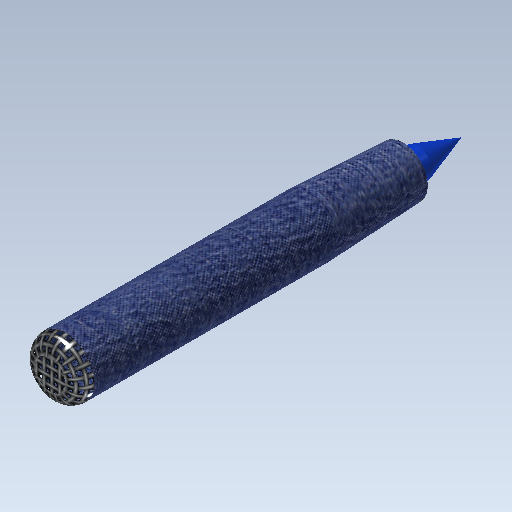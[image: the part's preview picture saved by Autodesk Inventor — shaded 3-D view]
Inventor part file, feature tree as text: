
AUTODESK INVENTOR PART (.ipt)
format: ipt  version: 2021.3 (Build 253353000, 353)  size: 197,120 bytes
history: native  units: mm
features: extrude x2, chamfer x2, sketch x2, fillet x1
ambient origin geometry x8: Origin, YZ Plane, XZ Plane, XY Plane, X Axis, Y Axis, Z Axis, Center Point
bodies: Solid1 (feature_tree)
feature tree (7):
  extrude  "Extrusion1"  Depth=120.0mm TaperAngle=0.0deg
  extrude  "Extrusion2"  Depth=5.0mm TaperAngle=0.0deg
  chamfer  "Chamfer1"  Distance=5.0mm Angle=45.0deg
  chamfer  "Chamfer2"  Distance=1.5mm Angle=45.0deg
  fillet  "Fillet1"  Radius=5.0mm
  sketch  "Sketch1"  dims[d0=20.0mm d1=120.0mm d2=0.0mm]
  sketch  "Sketch2"  dims[d3=10.0mm d4=20.0mm d5=0.0mm d6=5.0mm d7=15.0mm d8=45.0deg d9=1.5mm d10=32.75mm d11=45.0deg d12=5.0mm]
